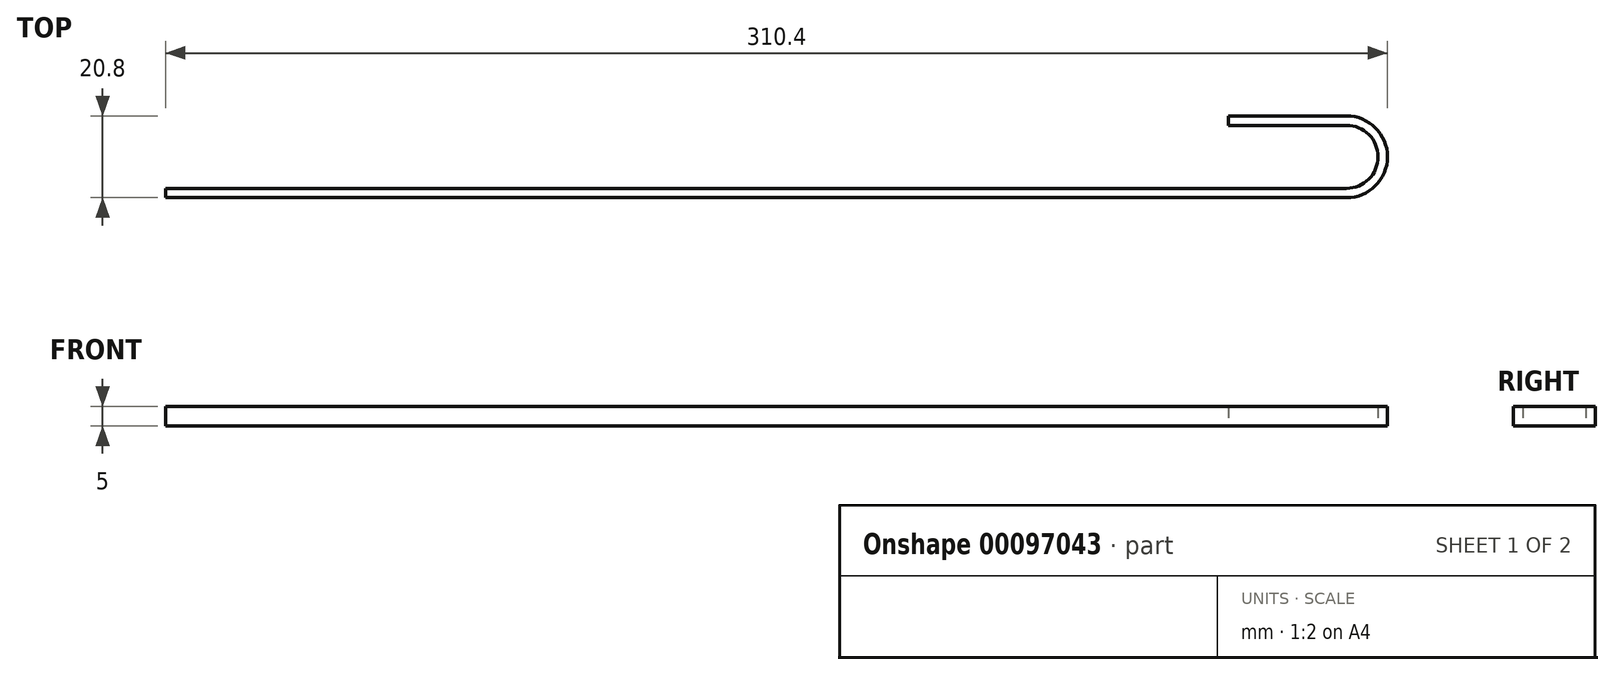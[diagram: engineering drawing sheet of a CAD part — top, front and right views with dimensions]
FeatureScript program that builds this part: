
annotation { "Feature Type Name" : "Feature", "Feature Type Description" : "" }
export const myFeature = defineFeature(function(context is Context, id is Id, definition is map)
    precondition{}
    {
        {
            var Q0;
            Q0=qCreatedBy(makeId("Top.planeOp"),FACE);
            var sketch = newSketch(context, id + "F0", { "sketchPlane" : qUnion([Q0])});
            skArc(sketch, "E0", {"start": v(0, -8) * mm, "mid": v(8, 0) * mm, "end": v(0, 8) * mm});
            skArc(sketch, "E1", {"start": v(0, -10.4) * mm, "mid": v(10.4, 0) * mm, "end": v(0, 10.4) * mm});
            skLineSegment(sketch, "E2", {"start": v(0, 10.4) * mm, "end": v(-30, 10.4) * mm});
            skLineSegment(sketch, "E3", {"start": v(-30, 10.4) * mm, "end": v(-30, 8) * mm});
            skLineSegment(sketch, "E4", {"start": v(-30, 8) * mm, "end": v(0, 8) * mm});
            skLineSegment(sketch, "E5.bottom", {"start": v(0, -8) * mm, "end": v(-300, -8) * mm});
            skLineSegment(sketch, "E5.top", {"start": v(0, -10.4) * mm, "end": v(-300, -10.4) * mm});
            skLineSegment(sketch, "E5.right", {"start": v(-300, -8) * mm, "end": v(-300, -10.4) * mm});
            skSolve(sketch);
        }
        {
            var Q0;
            Q0=qSketchRegion(id+"F0",true);
            extrude(context, id + "F1", {"entities" : qUnion([Q0]), "depth" : 5 * mm});
        }
    });
